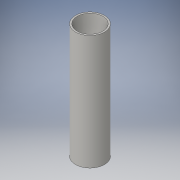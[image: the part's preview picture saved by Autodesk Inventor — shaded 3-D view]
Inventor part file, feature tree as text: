
AUTODESK INVENTOR PART (.ipt)
format: ipt  version: 2016 (Build 200138000, 138)  size: 91,648 bytes
history: native  units: in
note: dims shown in document units (in); Inventor stores cm internally (conversion verified against a paired STEP export)
features: extrude x1, sketch x1
ambient origin geometry x8: Origin, YZ Plane, XZ Plane, XY Plane, X Axis, Y Axis, Z Axis, Center Point
bodies: Solid1 (feature_tree)
feature tree (2):
  extrude  "Extrusion1"  Depth=17.814in
  sketch  "Sketch1"  dims[d0=4.496in d1=3.994in d2=17.814in d3=0.0in]
